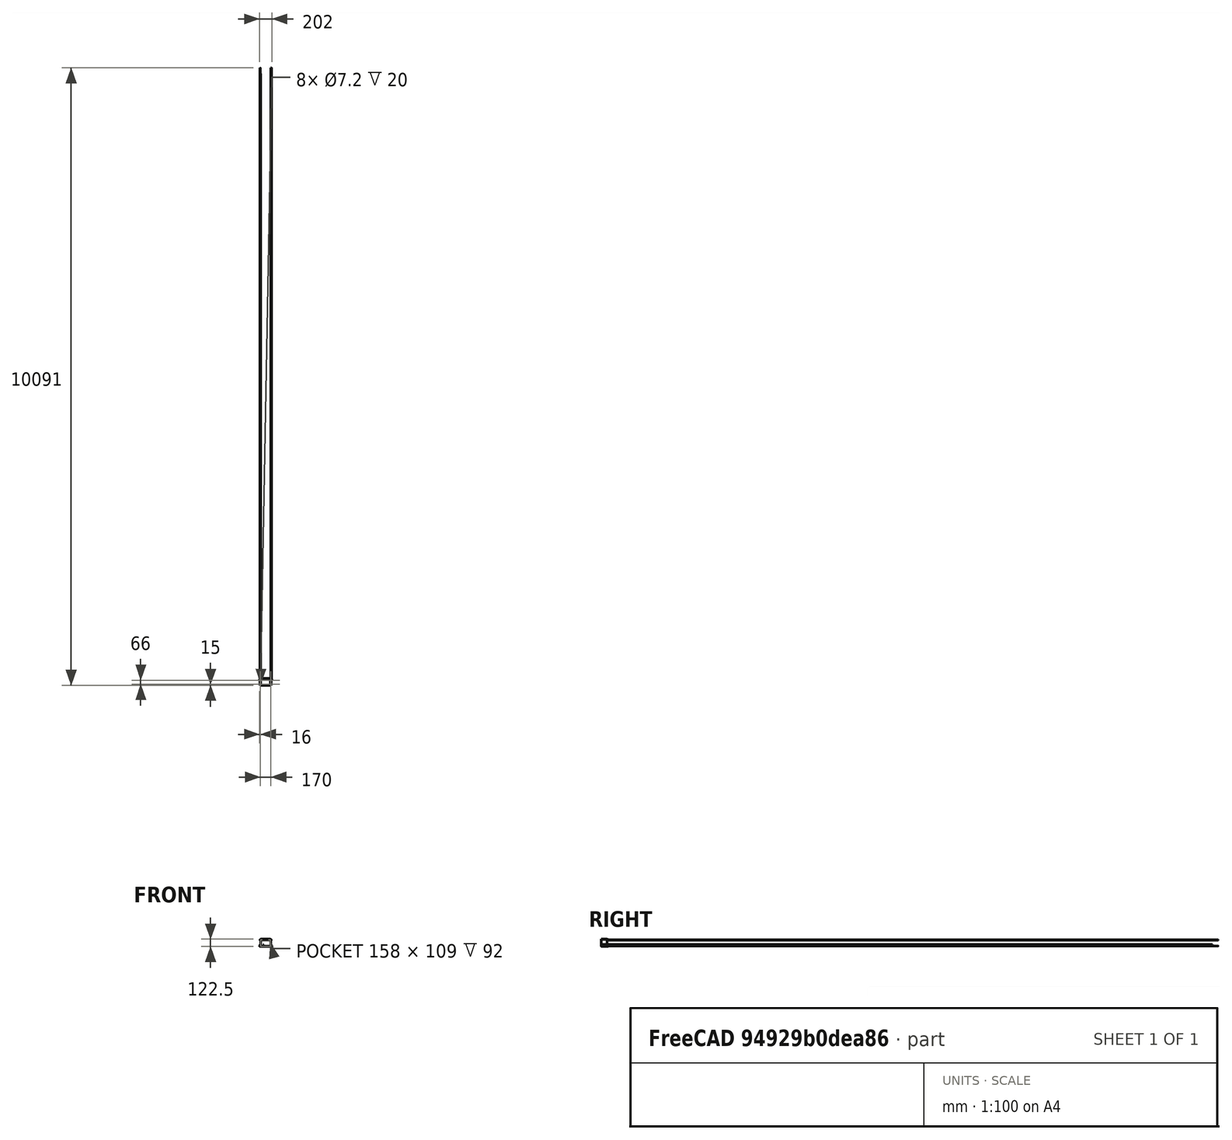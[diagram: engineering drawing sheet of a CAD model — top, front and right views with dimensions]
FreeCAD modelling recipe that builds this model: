
FCSTD DOCUMENT  (FreeCAD 0.15R4671 (Git))
Label: ElectronicsEnclosure
License: All rights reserved
LicenseURL: http://en.wikipedia.org/wiki/All_rights_reserved
objects: Sketcher::SketchObject×13, PartDesign::Pocket×8, Mesh::Feature×5, PartDesign::Pad×5, PartDesign::Fillet×5, Part::Feature×4
note: 48 computed .brp shape members not serialized (recipe doc carries the construction recipe); baked Part::Feature solids carry a one-line shape summary decoded from their .brp

FEATURE [Part::Feature] Part__Feature003  label="MKS_Gen_V1p3"
  Placement = pos=(4,-58,9) rot=(0,0,1;0rad)
  shape: bbox 143.1 x 84.2 x 22.31 mm, 8746 faces, 0 solids (baked)
FEATURE [Part::Feature] Part__Feature  label="OB1515_180mm"
  Placement = pos=(-90,0,0) rot=(0,1,0;1.5708rad)
  shape: bbox 180 x 15 x 15 mm, 158 faces (baked)
FEATURE [Part::Feature] Part__Feature004  label="OB1515_180mm001"
  Placement = pos=(-90,0,100) rot=(0,1,0;1.5708rad)
  shape: bbox 180 x 15 x 15 mm, 158 faces (baked)
FEATURE [Mesh::Feature] _0mmFan  label="40mmFan"
  Placement = pos=(15,-41,56) rot=(0,0,1;0rad)
FEATURE [Sketcher::SketchObject] Sketch
  Placement = pos=(0,0,-7.5) rot=(0,0,1;0rad)
  sketch-geometry (4):
    g0: LineSegment StartX=82 StartY=-8 StartZ=0 EndX=-82 EndY=-8 EndZ=0
    g1: LineSegment StartX=-82 StartY=-8 StartZ=0 EndX=-82 EndY=-106 EndZ=0
    g2: LineSegment StartX=-82 StartY=-106 StartZ=0 EndX=82 EndY=-106 EndZ=0
    g3: LineSegment StartX=82 StartY=-106 StartZ=0 EndX=82 EndY=-8 EndZ=0
  constraints (8):
    c: Coincident(g0,g1)
    c: Coincident(g1,g2)
    c: Coincident(g2,g3)
    c: Coincident(g3,g0)
    c: Horizontal(g0)
    c: Horizontal(g2)
    c: Vertical(g1)
    c: Vertical(g3)
FEATURE [PartDesign::Pad] Pad
  Length = 115
  Length2 = 100
  Placement = pos=(0,0,-7.5) rot=(0,0,1;0rad)
  Sketch = -> Sketch
  Type = 0
FEATURE [Sketcher::SketchObject] Sketch001
  Placement = pos=(0,0,107.5) rot=(0,0,1;0rad)
  Support = -> Pad [Face6]
  sketch-geometry (4):
    g0: LineSegment StartX=-79 StartY=-11 StartZ=0 EndX=79 EndY=-11 EndZ=0
    g1: LineSegment StartX=79 StartY=-11 StartZ=0 EndX=79 EndY=-103 EndZ=0
    g2: LineSegment StartX=79 StartY=-103 StartZ=0 EndX=-79 EndY=-103 EndZ=0
    g3: LineSegment StartX=-79 StartY=-103 StartZ=0 EndX=-79 EndY=-11 EndZ=0
  constraints (8):
    c: Coincident(g0,g1)
    c: Coincident(g1,g2)
    c: Coincident(g2,g3)
    c: Coincident(g3,g0)
    c: Horizontal(g0)
    c: Horizontal(g2)
    c: Vertical(g1)
    c: Vertical(g3)
FEATURE [PartDesign::Pocket] Pocket
  Length = 112
  Placement = pos=(0,0,-7.5) rot=(0,0,1;0rad)
  Sketch = -> Sketch001
  Type = 0
FEATURE [Sketcher::SketchObject] Sketch002
  Placement = pos=(0,0,-4.5) rot=(0,0,1;0rad)
  Support = -> Pocket [Face11]
  sketch-geometry (4):
    g0: Circle CenterX=71.2811 CenterY=-20.1362 CenterZ=0 NormalX=0 NormalY=0 NormalZ=1 Radius=4
    g1: Circle CenterX=71.2541 CenterY=-95.8403 CenterZ=0 NormalX=0 NormalY=0 NormalZ=1 Radius=4
    g2: Circle CenterX=-63.2692 CenterY=-95.845 CenterZ=0 NormalX=0 NormalY=0 NormalZ=1 Radius=4
    g3: Circle CenterX=-63.279 CenterY=-20.1649 CenterZ=0 NormalX=0 NormalY=0 NormalZ=1 Radius=4
  constraints (4):
    c: Radius(g0) = 4
    c: Equal(g0,g1)
    c: Equal(g0,g2)
    c: Equal(g0,g3)
FEATURE [PartDesign::Pad] Pad001
  Length = 13.5
  Length2 = 100
  Placement = pos=(0,0,-7.5) rot=(0,0,1;0rad)
  Sketch = -> Sketch002
  Type = 0
FEATURE [Sketcher::SketchObject] Sketch003
  Placement = pos=(0,0,9) rot=(0,0,1;0rad)
  Support = -> Pad001 [Face17]
  sketch-geometry (4):
    g0: Circle CenterX=-63.2989 CenterY=-20.1665 CenterZ=0 NormalX=0 NormalY=0 NormalZ=1 Radius=1.5
    g1: Circle CenterX=71.3054 CenterY=-20.1275 CenterZ=0 NormalX=0 NormalY=0 NormalZ=1 Radius=1.5
    g2: Circle CenterX=71.282 CenterY=-95.8363 CenterZ=0 NormalX=0 NormalY=0 NormalZ=1 Radius=1.5
    g3: Circle CenterX=-63.2831 CenterY=-95.8609 CenterZ=0 NormalX=0 NormalY=0 NormalZ=1 Radius=1.5
  constraints (4):
    c: Radius(g0) = 1.5
    c: Equal(g0,g1)
    c: Equal(g0,g2)
    c: Equal(g0,g3)
FEATURE [PartDesign::Pocket] Pocket001
  Length = 8
  Placement = pos=(0,0,-7.5) rot=(0,0,1;0rad)
  Sketch = -> Sketch003
  Type = 0
FEATURE [Sketcher::SketchObject] Sketch004
  Placement = pos=(0,0,107.5) rot=(0,0,1;0rad)
  Support = -> Pocket001 [Face5]
  sketch-geometry (4):
    g0: LineSegment StartX=-82 StartY=-106 StartZ=0 EndX=82 EndY=-106 EndZ=0
    g1: LineSegment StartX=82 StartY=-106 StartZ=0 EndX=82 EndY=-8 EndZ=0
    g2: LineSegment StartX=82 StartY=-8 StartZ=0 EndX=-82 EndY=-8 EndZ=0
    g3: LineSegment StartX=-82 StartY=-8 StartZ=0 EndX=-82 EndY=-106 EndZ=0
  constraints (8):
    c: Coincident(g0,g1)
    c: Coincident(g1,g2)
    c: Coincident(g2,g3)
    c: Coincident(g3,g0)
    c: Horizontal(g0)
    c: Horizontal(g2)
    c: Vertical(g1)
    c: Vertical(g3)
FEATURE [PartDesign::Pad] Pad002
  Length = 3
  Length2 = 100
  Placement = pos=(0,0,-7.5) rot=(0,0,1;0rad)
  Reversed = true
  Sketch = -> Sketch004
  Type = 0
FEATURE [Part::Feature] Pad002001  label="Pad003"
  shape: bbox 164 x 98 x 115 mm, 28 faces (baked)
FEATURE [Sketcher::SketchObject] Sketch005
  Placement = pos=(0,0,-7.5) rot=(1,0,0;3.14159rad)
  Support = -> Pad002001 [Face1]
  sketch-geometry (16):
    g0: ArcOfCircle CenterX=84 CenterY=25 CenterZ=0 NormalX=0 NormalY=0 NormalZ=1 Radius=7 StartAngle=4.71239 EndAngle=7.85398
    g1: ArcOfCircle CenterX=84 CenterY=91 CenterZ=0 NormalX=0 NormalY=0 NormalZ=1 Radius=7 StartAngle=4.71239 EndAngle=7.85398
    g2: ArcOfCircle CenterX=-84 CenterY=91 CenterZ=0 NormalX=0 NormalY=0 NormalZ=1 Radius=7 StartAngle=1.5708 EndAngle=4.71239
    g3: ArcOfCircle CenterX=-84 CenterY=25 CenterZ=0 NormalX=0 NormalY=0 NormalZ=1 Radius=7 StartAngle=1.5708 EndAngle=4.71239
    g4: LineSegment StartX=-84 StartY=32 StartZ=0 EndX=-81 EndY=32 EndZ=0
    g5: LineSegment StartX=-81 StartY=32 StartZ=0 EndX=-81 EndY=18 EndZ=0
    g6: LineSegment StartX=-81 StartY=18 StartZ=0 EndX=-84 EndY=18 EndZ=0
    g7: LineSegment StartX=-84 StartY=98 StartZ=0 EndX=-81 EndY=98 EndZ=0
    g8: LineSegment StartX=-81 StartY=98 StartZ=0 EndX=-81 EndY=84 EndZ=0
    g9: LineSegment StartX=-81 StartY=84 StartZ=0 EndX=-84 EndY=84 EndZ=0
    g10: LineSegment StartX=84 StartY=98 StartZ=0 EndX=81 EndY=98 EndZ=0
    g11: LineSegment StartX=81 StartY=98 StartZ=0 EndX=81 EndY=84 EndZ=0
    g12: LineSegment StartX=81 StartY=84 StartZ=0 EndX=84 EndY=84 EndZ=0
    g13: LineSegment StartX=84 StartY=32 StartZ=0 EndX=81 EndY=32 EndZ=0
    g14: LineSegment StartX=81 StartY=32 StartZ=0 EndX=81 EndY=18 EndZ=0
    g15: LineSegment StartX=81 StartY=18 StartZ=0 EndX=84 EndY=18 EndZ=0
  constraints (25):
    c: Tangent(g3,g4) = 1.5708
    c: Coincident(g4,g5)
    c: Vertical(g5)
    c: Coincident(g5,g6)
    c: Coincident(g6,g3)
    c: Horizontal(g6)
    c: Tangent(g6,g3)
    c: Tangent(g2,g7) = 1.5708
    c: Coincident(g7,g8)
    c: Vertical(g8)
    c: Coincident(g8,g9)
    c: Coincident(g9,g2)
    c: Horizontal(g9)
    c: Tangent(g1,g10) = -1.5708
    c: Coincident(g10,g11)
    c: Vertical(g11)
    c: Coincident(g11,g12)
    c: Coincident(g12,g1)
    c: Horizontal(g12)
    c: Tangent(g0,g13) = -1.5708
    c: Coincident(g13,g14)
    c: Vertical(g14)
    c: Coincident(g14,g15)
    c: Coincident(g15,g0)
    c: Horizontal(g15)
FEATURE [PartDesign::Pad] Pad002002
  Length = 35
  Length2 = 100
  Reversed = true
  Sketch = -> Sketch005
  Type = 0
FEATURE [PartDesign::Fillet] Fillet
  Base = -> Pad002002 [Edge28,Edge26,Edge22,Edge24,Edge8,Edge12,Edge14,Edge10]
  Radius = 1.99
FEATURE [Sketcher::SketchObject] Sketch006
  Placement = pos=(0,-106,0) rot=(1,0,0;1.5708rad)
  Support = -> Fillet [Face7]
  sketch-geometry (10):
    g0: LineSegment StartX=-82 StartY=29 StartZ=0 EndX=-82 EndY=27 EndZ=0
    g1: LineSegment StartX=-82 StartY=27 StartZ=0 EndX=-91 EndY=18 EndZ=0
    g2: LineSegment StartX=-91 StartY=18 StartZ=0 EndX=-92 EndY=18 EndZ=0
    g3: LineSegment StartX=-92 StartY=18 StartZ=0 EndX=-92 EndY=29 EndZ=0
    g4: LineSegment StartX=-92 StartY=29 StartZ=0 EndX=-82 EndY=29 EndZ=0
    g5: LineSegment StartX=82 StartY=29 StartZ=0 EndX=82 EndY=27 EndZ=0
    g6: LineSegment StartX=82 StartY=27 StartZ=0 EndX=91 EndY=18 EndZ=0
    g7: LineSegment StartX=91 StartY=18 StartZ=0 EndX=92 EndY=18 EndZ=0
    g8: LineSegment StartX=92 StartY=18 StartZ=0 EndX=92 EndY=29 EndZ=0
    g9: LineSegment StartX=92 StartY=29 StartZ=0 EndX=82 EndY=29 EndZ=0
  constraints (18):
    c: Vertical(g0)
    c: Coincident(g0,g1)
    c: Coincident(g1,g2)
    c: Horizontal(g2)
    c: Coincident(g2,g3)
    c: Vertical(g3)
    c: Coincident(g3,g4)
    c: Coincident(g4,g0)
    c: Horizontal(g4)
    c: Vertical(g5)
    c: Coincident(g5,g6)
    c: Coincident(g6,g7)
    c: Horizontal(g7)
    c: Coincident(g7,g8)
    c: Vertical(g8)
    c: Coincident(g8,g9)
    c: Coincident(g9,g5)
    c: Horizontal(g9)
FEATURE [PartDesign::Pocket] Pocket002
  Length = 5
  Sketch = -> Sketch006
  Type = 1
FEATURE [Mesh::Feature] HexNutStyle1_M3
  Placement = pos=(86.28,1.15,-100) rot=(0,0,1;0.523599rad)
FEATURE [Mesh::Feature] HexNutStyle1_M
  Placement = pos=(86.28,-64.85,-100) rot=(0,0,1;0.523599rad)
FEATURE [Mesh::Feature] HexNutStyle1_M004
  Placement = pos=(-83.72,1.15,-100) rot=(0,0,1;0.523599rad)
FEATURE [Mesh::Feature] HexNutStyle1_M005
  Placement = pos=(-83.72,-64.85,-100) rot=(0,0,1;0.523599rad)
FEATURE [Sketcher::SketchObject] Sketch007
  Placement = pos=(0,0,-7.5) rot=(1,0,0;3.14159rad)
  Support = -> Pocket002 [Face2]
  sketch-geometry (4):
    g0: Circle CenterX=-85 CenterY=91 CenterZ=0 NormalX=0 NormalY=0 NormalZ=1 Radius=1.8
    g1: Circle CenterX=-85 CenterY=25 CenterZ=0 NormalX=0 NormalY=0 NormalZ=1 Radius=1.8
    g2: Circle CenterX=85 CenterY=25 CenterZ=0 NormalX=0 NormalY=0 NormalZ=1 Radius=1.8
    g3: Circle CenterX=85 CenterY=91 CenterZ=0 NormalX=0 NormalY=0 NormalZ=1 Radius=1.8
  constraints (4):
    c: Radius(g0) = 1.8
    c: Equal(g0,g1)
    c: Equal(g0,g2)
    c: Equal(g0,g3)
FEATURE [PartDesign::Pocket] Pocket003
  Length = 28
  Sketch = -> Sketch007
  Type = 0
FEATURE [Sketcher::SketchObject] Sketch008
  Placement = pos=(0,0,-7.5) rot=(1,0,0;3.14159rad)
  Support = -> Pocket003 [Face2]
  sketch-geometry (4):
    g0: Circle CenterX=85 CenterY=91 CenterZ=0 NormalX=0 NormalY=0 NormalZ=1 Radius=3.6
    g1: Circle CenterX=85 CenterY=25 CenterZ=0 NormalX=0 NormalY=0 NormalZ=1 Radius=3.6
    g2: Circle CenterX=-85 CenterY=91 CenterZ=0 NormalX=0 NormalY=0 NormalZ=1 Radius=3.6
    g3: Circle CenterX=-85 CenterY=25 CenterZ=0 NormalX=0 NormalY=0 NormalZ=1 Radius=3.6
  constraints (4):
    c: Radius(g0) = 3.6
    c: Equal(g0,g1)
    c: Equal(g0,g2)
    c: Equal(g0,g3)
FEATURE [PartDesign::Pocket] Pocket004
  Length = 20
  Sketch = -> Sketch008
  Type = 0
FEATURE [Sketcher::SketchObject] Sketch009
  Placement = pos=(0,-8,0) rot=(0,0.707107,0.707107;3.14159rad)
  Support = -> Pocket004 [Face1]
  sketch-geometry (16):
    g0: LineSegment StartX=-81 StartY=7.5 StartZ=0 EndX=-101 EndY=7.5 EndZ=0
    g1: LineSegment StartX=-101 StartY=7.5 StartZ=0 EndX=-101 EndY=-7.5 EndZ=0
    g2: LineSegment StartX=-101 StartY=-7.5 StartZ=0 EndX=-81 EndY=-7.5 EndZ=0
    g3: LineSegment StartX=-81 StartY=-7.5 StartZ=0 EndX=-81 EndY=7.5 EndZ=0
    g4: LineSegment StartX=81 StartY=7.5 StartZ=0 EndX=101 EndY=7.5 EndZ=0
    g5: LineSegment StartX=101 StartY=7.5 StartZ=0 EndX=101 EndY=-7.5 EndZ=0
    g6: LineSegment StartX=101 StartY=-7.5 StartZ=0 EndX=81 EndY=-7.5 EndZ=0
    g7: LineSegment StartX=81 StartY=-7.5 StartZ=0 EndX=81 EndY=7.5 EndZ=0
    g8: LineSegment StartX=-92 StartY=107.5 StartZ=0 EndX=-81 EndY=107.5 EndZ=0
    g9: LineSegment StartX=-81 StartY=107.5 StartZ=0 EndX=-81 EndY=92.5 EndZ=0
    g10: LineSegment StartX=-81 StartY=92.5 StartZ=0 EndX=-92 EndY=92.5 EndZ=0
    g11: LineSegment StartX=-92 StartY=92.5 StartZ=0 EndX=-92 EndY=107.5 EndZ=0
    g12: LineSegment StartX=81 StartY=92.5 StartZ=0 EndX=92 EndY=92.5 EndZ=0
    g13: LineSegment StartX=92 StartY=92.5 StartZ=0 EndX=92 EndY=107.5 EndZ=0
    g14: LineSegment StartX=92 StartY=107.5 StartZ=0 EndX=81 EndY=107.5 EndZ=0
    g15: LineSegment StartX=81 StartY=107.5 StartZ=0 EndX=81 EndY=92.5 EndZ=0
  constraints (32):
    c: Coincident(g0,g1)
    c: Coincident(g1,g2)
    c: Coincident(g2,g3)
    c: Coincident(g3,g0)
    c: Horizontal(g0)
    c: Horizontal(g2)
    c: Vertical(g1)
    c: Vertical(g3)
    c: Coincident(g4,g5)
    c: Coincident(g5,g6)
    c: Coincident(g6,g7)
    c: Coincident(g7,g4)
    c: Horizontal(g4)
    c: Horizontal(g6)
    c: Vertical(g5)
    c: Vertical(g7)
    c: Coincident(g8,g9)
    c: Coincident(g9,g10)
    c: Coincident(g10,g11)
    c: Coincident(g11,g8)
    c: Horizontal(g8)
    c: Horizontal(g10)
    c: Vertical(g9)
    c: Vertical(g11)
    c: Coincident(g12,g13)
    c: Coincident(g13,g14)
    c: Coincident(g14,g15)
    c: Coincident(g15,g12)
    c: Horizontal(g12)
    c: Horizontal(g14)
    c: Vertical(g13)
    c: Vertical(g15)
FEATURE [PartDesign::Pad] Pad002003
  Length = 7
  Length2 = 100
  Reversed = true
  Sketch = -> Sketch009
  Type = 0
FEATURE [PartDesign::Fillet] Fillet001
  Base = -> Pad002003 [Edge22,Edge63]
  Radius = 4
FEATURE [PartDesign::Fillet] Fillet002
  Base = -> Fillet001 [Edge111,Edge77,Edge88,Edge51,Edge112,Edge78,Edge128,Edge92]
  Radius = 4
FEATURE [PartDesign::Fillet] Fillet003
  Base = -> Fillet002 [Edge120,Edge46]
  Radius = 4
FEATURE [Sketcher::SketchObject] Sketch010
  Placement = pos=(0,-15,0) rot=(1,0,0;1.5708rad)
  Support = -> Fillet003 [Face35]
  sketch-geometry (4):
    g0: Circle CenterX=-87.5 CenterY=100 CenterZ=0 NormalX=0 NormalY=0 NormalZ=1 Radius=1.8
    g1: Circle CenterX=87.5 CenterY=100 CenterZ=0 NormalX=0 NormalY=0 NormalZ=1 Radius=1.8
    g2: Circle CenterX=95 CenterY=0 CenterZ=0 NormalX=0 NormalY=0 NormalZ=1 Radius=1.8
    g3: Circle CenterX=-95 CenterY=0 CenterZ=0 NormalX=0 NormalY=0 NormalZ=1 Radius=1.8
  constraints (6):
    c: PointOnObject(g2,g-1)
    c: PointOnObject(g3,g-1)
    c: Radius(g0) = 1.8
    c: Equal(g0,g1)
    c: Equal(g0,g2)
    c: Equal(g0,g3)
FEATURE [PartDesign::Pocket] Pocket005
  Length = 5
  Sketch = -> Sketch010
  Type = 1
FEATURE [Sketcher::SketchObject] Sketch011
  Placement = pos=(0,-15,0) rot=(1,0,0;1.5708rad)
  Support = -> Pocket005 [Face31]
  sketch-geometry (4):
    g0: Circle CenterX=-87.5 CenterY=100 CenterZ=0 NormalX=0 NormalY=0 NormalZ=1 Radius=3.5
    g1: Circle CenterX=87.5 CenterY=100 CenterZ=0 NormalX=0 NormalY=0 NormalZ=1 Radius=3.5
    g2: Circle CenterX=95 CenterY=0 CenterZ=0 NormalX=0 NormalY=0 NormalZ=1 Radius=3.5
    g3: Circle CenterX=-95 CenterY=0 CenterZ=0 NormalX=0 NormalY=0 NormalZ=1 Radius=3.5
  constraints (6):
    c: PointOnObject(g2,g-1)
    c: PointOnObject(g3,g-1)
    c: Radius(g0) = 3.5
    c: Equal(g0,g1)
    c: Equal(g0,g2)
    c: Equal(g0,g3)
FEATURE [PartDesign::Pocket] Pocket006
  Length = 3
  Sketch = -> Sketch011
  Type = 0
FEATURE [PartDesign::Fillet] Fillet004
  Base = -> Pocket006 [Edge49,Edge45,Edge78,Edge79,Edge139]
  Radius = 1
FEATURE [Sketcher::SketchObject] Sketch012
  Placement = pos=(0,-106,0) rot=(1,0,0;1.5708rad)
  Support = -> Fillet004 [Face26]
  sketch-geometry (4):
    g0: LineSegment StartX=-46 StartY=21.5 StartZ=0 EndX=-33.5 EndY=21.5 EndZ=0
    g1: LineSegment StartX=-33.5 StartY=21.5 StartZ=0 EndX=-33.5 EndY=10.5 EndZ=0
    g2: LineSegment StartX=-33.5 StartY=10.5 StartZ=0 EndX=-46 EndY=10.5 EndZ=0
    g3: LineSegment StartX=-46 StartY=10.5 StartZ=0 EndX=-46 EndY=21.5 EndZ=0
  constraints (8):
    c: Coincident(g0,g1)
    c: Coincident(g1,g2)
    c: Coincident(g2,g3)
    c: Coincident(g3,g0)
    c: Horizontal(g0)
    c: Horizontal(g2)
    c: Vertical(g1)
    c: Vertical(g3)
FEATURE [PartDesign::Pocket] Pocket007
  Length = 5
  Sketch = -> Sketch012
  Type = 0
